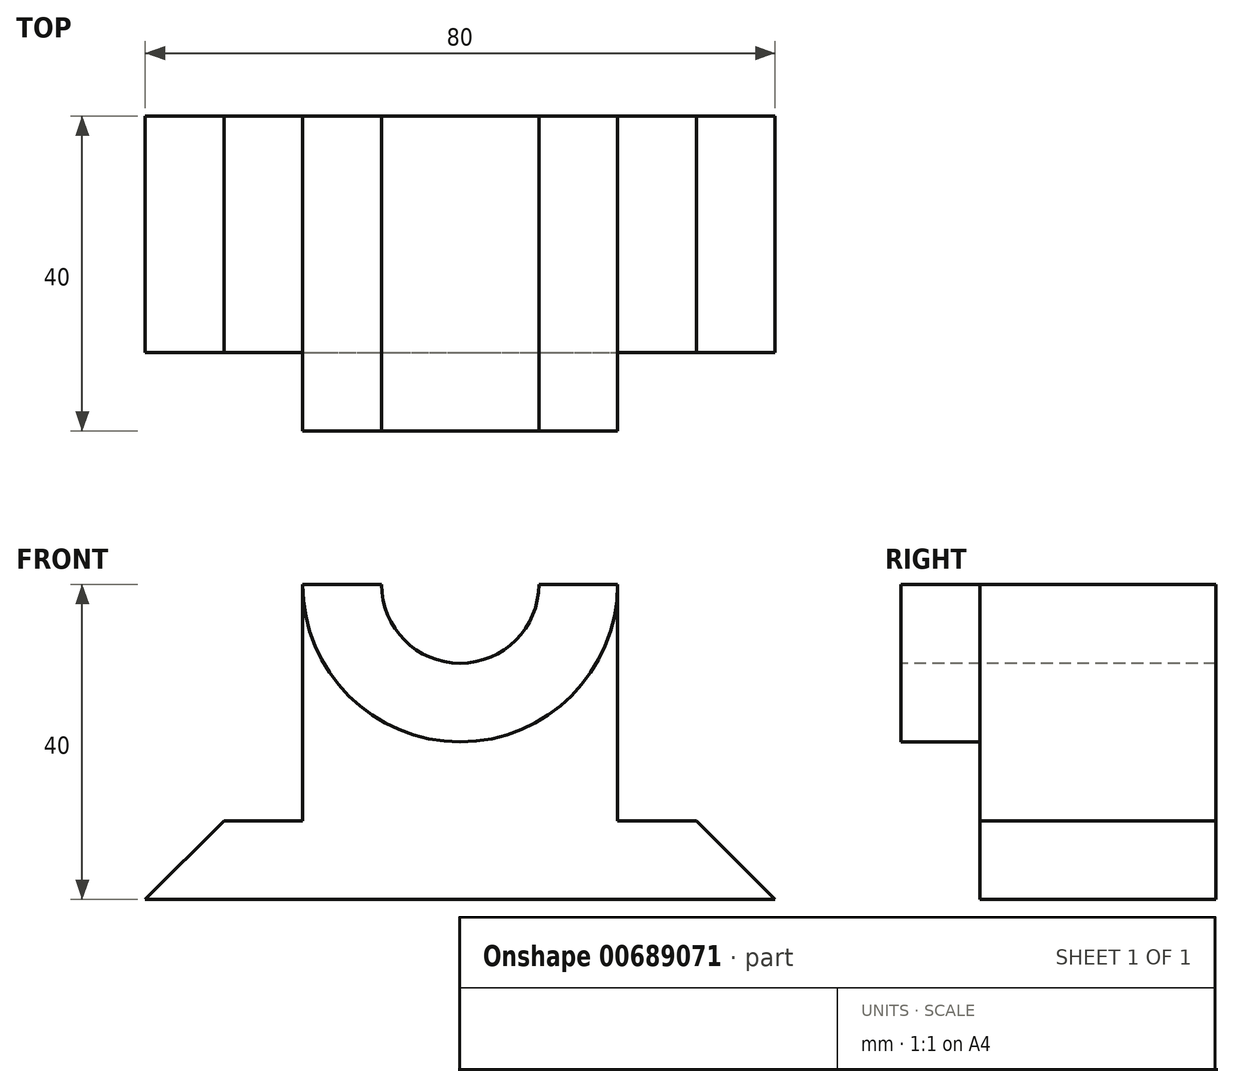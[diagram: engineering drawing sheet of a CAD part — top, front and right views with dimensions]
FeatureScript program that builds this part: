
annotation { "Feature Type Name" : "Feature", "Feature Type Description" : "" }
export const myFeature = defineFeature(function(context is Context, id is Id, definition is map)
    precondition{}
    {
        {
            var Q0;
            Q0=qCreatedBy(makeId("Front.planeOp"),FACE);
            var sketch = newSketch(context, id + "F0", { "sketchPlane" : qUnion([Q0])});
            skLineSegment(sketch, "E0", {"start": v(0, 0) * mm, "end": v(80, 0) * mm});
            skLineSegment(sketch, "E1", {"start": v(80, 0) * mm, "end": v(70, 10) * mm});
            skLineSegment(sketch, "E2", {"start": v(70, 10) * mm, "end": v(60, 10) * mm});
            skLineSegment(sketch, "E3", {"start": v(60, 10) * mm, "end": v(60, 40) * mm});
            skLineSegment(sketch, "E4", {"start": v(20, 10) * mm, "end": v(10, 10) * mm});
            skLineSegment(sketch, "E5", {"start": v(10, 10) * mm, "end": v(0, 0) * mm});
            skLineSegment(sketch, "E6", {"start": v(60, 40) * mm, "end": v(20, 40) * mm});
            skLineSegment(sketch, "E7", {"start": v(20, 40) * mm, "end": v(20, 10) * mm});
            skSolve(sketch);
        }
        {
            var Q0;
            Q0=makeQuery(id+"F0.imprint","IMPRINT",FACE,{"disambiguationData":[TD([[makeQuery(id+"F0.imprint","IMPRINT",EDGE,{"derivedFrom":sQuery(id+"F0.wireOp",EDGE,"E0")}),1.0]])]});
            extrude(context, id + "F1", {"entities" : qUnion([Q0]), "depth" : 30 * mm, "offsetDistance" : 25 * mm});
        }
        {
            var Q0;
            Q0=makeQuery(id+"F1.opExtrude","CAP_FACE",FACE,{"disambiguationData":[OSD([sQuery(id+"F0.wireOp",EDGE,"E0"),sQuery(id+"F0.wireOp",EDGE,"E1"),sQuery(id+"F0.wireOp",EDGE,"E2"),sQuery(id+"F0.wireOp",EDGE,"E3"),sQuery(id+"F0.wireOp",EDGE,"E4"),sQuery(id+"F0.wireOp",EDGE,"E5"),sQuery(id+"F0.wireOp",EDGE,"E6"),sQuery(id+"F0.wireOp",EDGE,"E7")])],"isStart":false});
            var sketch = newSketch(context, id + "F2", { "sketchPlane" : qUnion([Q0])});
            skArc(sketch, "E8", {"start": v(60, 40) * mm, "mid": v(40, 20) * mm, "end": v(20, 40) * mm});
            skLineSegment(sketch, "E9", {"start": v(20, 40) * mm, "end": v(60, 40) * mm});
            skSolve(sketch);
        }
        {
            var Q0;
            Q0 = qSketchRegion(id + "F2", true);
            extrude(context, id + "F3", {"entities" : qUnion([Q0]), "operationType" : NewBodyOperationType.ADD, "depth" : 10 * mm, "offsetDistance" : 25 * mm});
        }
        {
            var Q0;
            Q0=makeQuery(id+"F3.opExtrude","CAP_FACE",FACE,{"disambiguationData":[OSD([sQuery(id+"F2.wireOp",EDGE,"E8"),sQuery(id+"F2.wireOp",EDGE,"E9")])],"isStart":false});
            var sketch = newSketch(context, id + "F4", { "sketchPlane" : qUnion([Q0])});
            skArc(sketch, "E10", {"start": v(50, 40) * mm, "mid": v(40, 30) * mm, "end": v(30, 40) * mm});
            skLineSegment(sketch, "E11", {"start": v(30, 40) * mm, "end": v(50, 40) * mm});
            skSolve(sketch);
        }
        {
            var Q0;
            Q0 = qSketchRegion(id + "F4", true);
            extrude(context, id + "F5", {"entities" : qUnion([Q0]), "operationType" : NewBodyOperationType.REMOVE, "endBound" : BoundingType.THROUGH_ALL, "oppositeDirection" : true, "depth" : 25 * mm, "offsetDistance" : 25 * mm});
        }
    });
